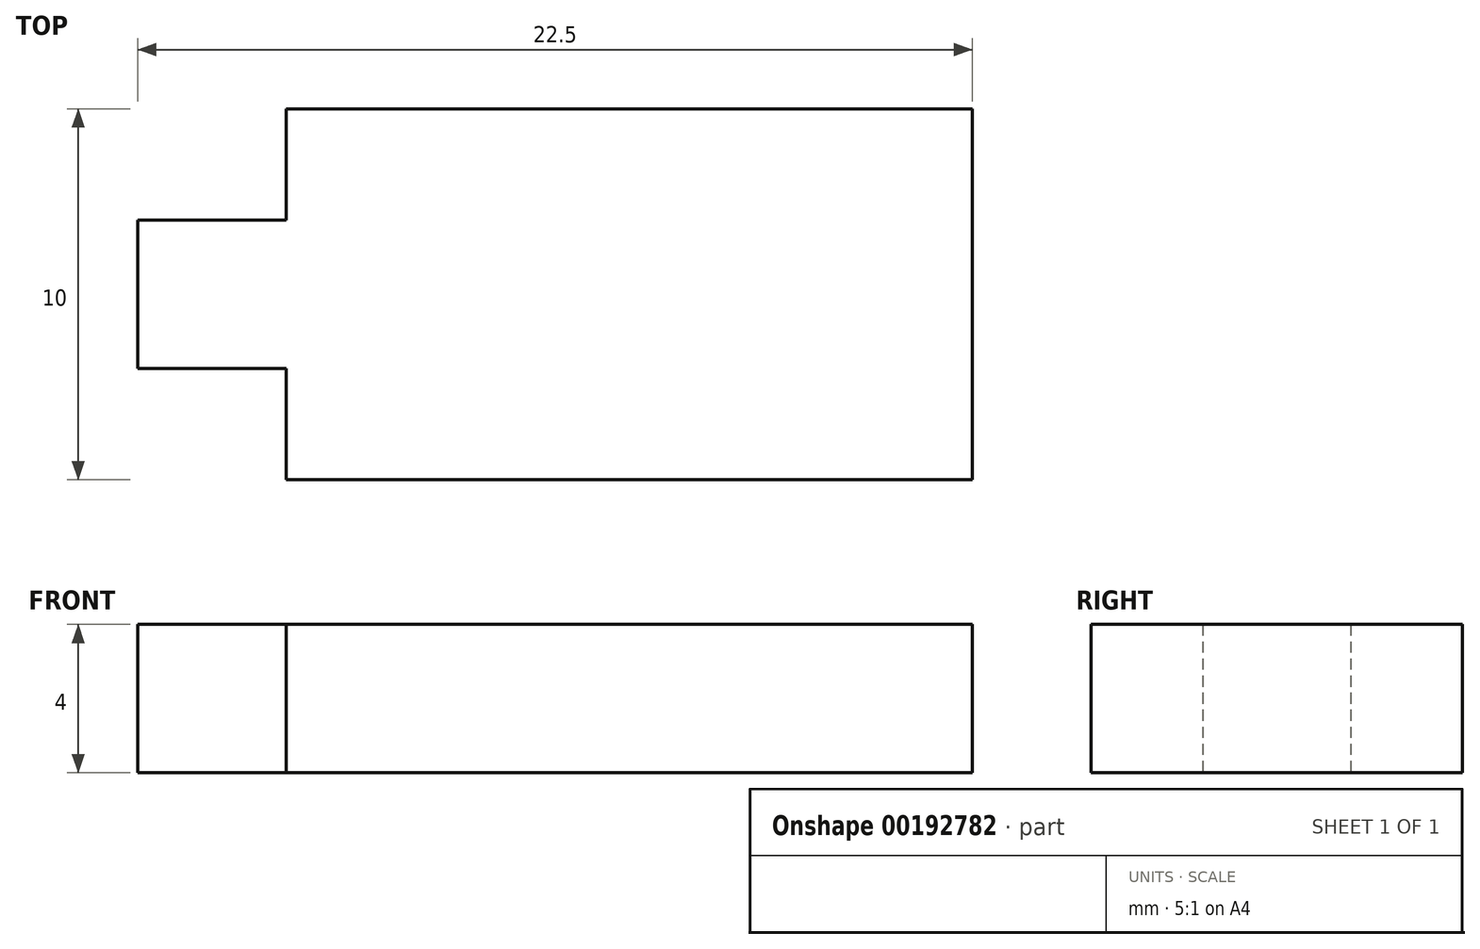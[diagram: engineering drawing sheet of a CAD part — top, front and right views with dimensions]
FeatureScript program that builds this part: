
annotation { "Feature Type Name" : "Feature", "Feature Type Description" : "" }
export const myFeature = defineFeature(function(context is Context, id is Id, definition is map)
    precondition{}
    {
        {
            var Q0;
            Q0=qCreatedBy(makeId("Top.planeOp"),FACE);
            var sketch = newSketch(context, id + "F0", { "sketchPlane" : qUnion([Q0])});
            skLineSegment(sketch, "E0.bottom", {"start": v(-13.25, -2) * mm, "end": v(-9.25, -2) * mm});
            skLineSegment(sketch, "E0.top", {"start": v(-13.25, 2) * mm, "end": v(-9.25, 2) * mm});
            skLineSegment(sketch, "E0.left", {"start": v(-13.25, -2) * mm, "end": v(-13.25, 2) * mm});
            skLineSegment(sketch, "E0.right", {"start": v(-9.25, -2) * mm, "end": v(-9.25, 2) * mm});
            skPoint(sketch, "E0.middle", {"position": v(-11.25, 0) * mm});
            skLineSegment(sketch, "E1.bottom", {"start": v(-9.25, -5) * mm, "end": v(9.25, -5) * mm});
            skLineSegment(sketch, "E1.top", {"start": v(-9.25, 5) * mm, "end": v(9.25, 5) * mm});
            skLineSegment(sketch, "E1.left", {"start": v(-9.25, -5) * mm, "end": v(-9.25, 5) * mm});
            skLineSegment(sketch, "E1.right", {"start": v(9.25, -5) * mm, "end": v(9.25, 5) * mm});
            skPoint(sketch, "E1.middle", {"position": v(0, 0) * mm});
            skSolve(sketch);
        }
        {
            var Q0;
            Q0 = qSketchRegion(id + "F0", true);
            extrude(context, id + "F1", {"entities" : qUnion([Q0]), "depth" : 4 * mm});
        }
    });
